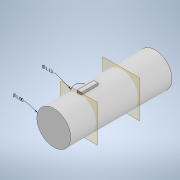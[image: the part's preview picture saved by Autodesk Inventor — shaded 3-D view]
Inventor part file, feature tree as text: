
AUTODESK INVENTOR PART (.ipt)
format: ipt  version: 2021 (Build 250183000, 183)  size: 130,048 bytes
history: native  units: in
note: dims shown in document units (in); Inventor stores cm internally (conversion verified against a paired STEP export)
features: other x3, extrude x3, sketch x3, plane x2
ambient origin geometry x8: Origin, YZ Plane, XZ Plane, XY Plane, X Axis, Y Axis, Z Axis, Center Point
bodies: Solid1 (feature_tree)
feature tree (11):
  other  "Annotations"
  extrude  "Extrusion1"  Depth=3.0in TaperAngle=0.0deg
  plane  "WorkPlaneForFirstKeys"
  extrude  "Extrusion2"  Depth=1.125in
  plane  "WorkPlaneForSecondKeys"
  extrude  "Extrusion3"  Depth=1.0in
  sketch  "Sketch1"  dims[d0=1.0in d1=3.0in d2=0.0in]
  sketch  "Sketch3"  dims[d3=-0.75in d4=1.125in]
  sketch  "Sketch4"  dims[d6=0.0625in d7=0.0625in d8=0.5in d9=0.0in d10=-2.0in d11=1.25in d12=0.0625in d13=0.0625in d14=0.5in d15=0.0in d16=1.1172in d17=1.0in d18=2.3985in d19=0.2232in d20=0.1525in d21=1.125in]
  other  "Diameter Dimension 1"
  other  "Diameter Dimension 2"
